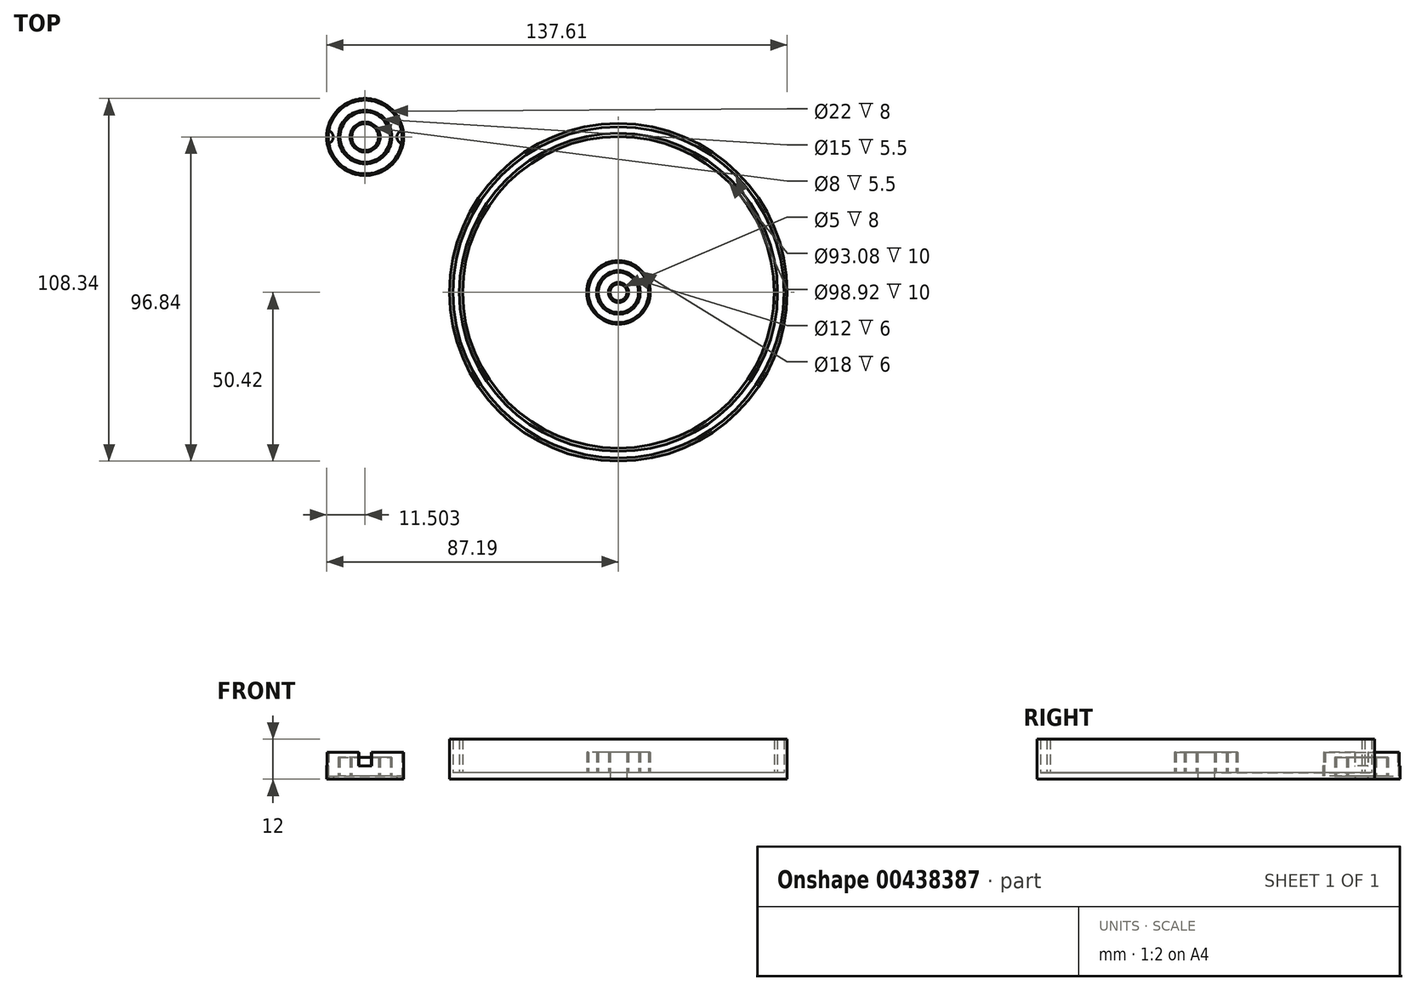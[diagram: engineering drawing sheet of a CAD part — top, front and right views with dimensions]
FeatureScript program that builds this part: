
annotation { "Feature Type Name" : "Feature", "Feature Type Description" : "" }
export const myFeature = defineFeature(function(context is Context, id is Id, definition is map)
    precondition{}
    {
        {
            var Q0;
            Q0=qCreatedBy(makeId("Top.planeOp"),FACE);
            var sketch = newSketch(context, id + "F0", { "sketchPlane" : qUnion([Q0])});
            skCircle(sketch, "E0", {"center": v(0, 0) * mm, "radius": 47.5 * mm});
            skCircle(sketch, "E1", {"center": v(0, 0) * mm, "radius": 49.46 * mm});
            skCircle(sketch, "E2", {"center": v(0, 0) * mm, "radius": 50.42 * mm});
            skCircle(sketch, "E3", {"center": v(0, 0) * mm, "radius": 46.54 * mm});
            skCircle(sketch, "E4", {"center": v(0, 0) * mm, "radius": 2.5 * mm});
            skCircle(sketch, "E5", {"center": v(0, 0) * mm, "radius": 3 * mm});
            skCircle(sketch, "E6", {"center": v(0, 0) * mm, "radius": 6 * mm});
            skCircle(sketch, "E7", {"center": v(0, 0) * mm, "radius": 6.5 * mm});
            skCircle(sketch, "E8", {"center": v(0, 0) * mm, "radius": 9 * mm});
            skCircle(sketch, "E9", {"center": v(0, 0) * mm, "radius": 9.5 * mm});
            skSolve(sketch);
        }
        {
            var Q0;
            Q0=makeQuery(id+"F0.imprint","IMPRINT",FACE,{"disambiguationData":[TD([[makeQuery(id+"F0.imprint","IMPRINT",EDGE,{"derivedFrom":sQuery(id+"F0.wireOp",EDGE,"E0")}),1.0]])]});
            var Q1;
            Q1=makeQuery(id+"F0.imprint","IMPRINT",FACE,{"disambiguationData":[TD([[makeQuery(id+"F0.imprint","IMPRINT",EDGE,{"derivedFrom":sQuery(id+"F0.wireOp",EDGE,"E1")}),-1.0]])]});
            var Q2;
            Q2=makeQuery(id+"F0.imprint","IMPRINT",FACE,{"disambiguationData":[TD([[makeQuery(id+"F0.imprint","IMPRINT",EDGE,{"derivedFrom":sQuery(id+"F0.wireOp",EDGE,"E0")}),-1.0]])]});
            var Q3;
            Q3=makeQuery(id+"F0.imprint","IMPRINT",FACE,{"disambiguationData":[TD([[makeQuery(id+"F0.imprint","IMPRINT",EDGE,{"derivedFrom":sQuery(id+"F0.wireOp",EDGE,"E3")}),1.0]])]});
            var Q4;
            Q4=makeQuery(id+"F0.imprint","IMPRINT",FACE,{"disambiguationData":[TD([[makeQuery(id+"F0.imprint","IMPRINT",EDGE,{"derivedFrom":sQuery(id+"F0.wireOp",EDGE,"E7")}),-1.0]])]});
            var Q5;
            Q5=makeQuery(id+"F0.imprint","IMPRINT",FACE,{"disambiguationData":[TD([[makeQuery(id+"F0.imprint","IMPRINT",EDGE,{"derivedFrom":sQuery(id+"F0.wireOp",EDGE,"E5")}),-1.0]])]});
            var Q6;
            Q6=makeQuery(id+"F0.imprint","IMPRINT",FACE,{"disambiguationData":[TD([[makeQuery(id+"F0.imprint","IMPRINT",EDGE,{"derivedFrom":sQuery(id+"F0.wireOp",EDGE,"E4")}),-1.0]])]});
            var Q7;
            Q7=makeQuery(id+"F0.imprint","IMPRINT",FACE,{"disambiguationData":[TD([[makeQuery(id+"F0.imprint","IMPRINT",EDGE,{"derivedFrom":sQuery(id+"F0.wireOp",EDGE,"E6")}),-1.0]])]});
            var Q8;
            Q8=makeQuery(id+"F0.imprint","IMPRINT",FACE,{"disambiguationData":[TD([[makeQuery(id+"F0.imprint","IMPRINT",EDGE,{"derivedFrom":sQuery(id+"F0.wireOp",EDGE,"E8")}),-1.0]])]});
            extrude(context, id + "F1", {"entities" : qUnion([Q0, Q1, Q2, Q3, Q4, Q5, Q6, Q7, Q8]), "depth" : 2 * mm, "offsetDistance" : 25 * mm});
        }
        {
            var Q0;
            Q0=makeQuery(id+"F0.imprint","IMPRINT",FACE,{"disambiguationData":[TD([[makeQuery(id+"F0.imprint","IMPRINT",EDGE,{"derivedFrom":sQuery(id+"F0.wireOp",EDGE,"E1")}),-1.0]])]});
            var Q1;
            Q1=makeQuery(id+"F0.imprint","IMPRINT",FACE,{"disambiguationData":[TD([[makeQuery(id+"F0.imprint","IMPRINT",EDGE,{"derivedFrom":sQuery(id+"F0.wireOp",EDGE,"E0")}),1.0]])]});
            extrude(context, id + "F2", {"entities" : qUnion([Q0, Q1]), "operationType" : NewBodyOperationType.ADD, "depth" : 12 * mm, "offsetDistance" : 25 * mm});
        }
        {
            var Q0;
            Q0=makeQuery(id+"F0.imprint","IMPRINT",FACE,{"disambiguationData":[TD([[makeQuery(id+"F0.imprint","IMPRINT",EDGE,{"derivedFrom":sQuery(id+"F0.wireOp",EDGE,"E8")}),-1.0]])]});
            var Q1;
            Q1=makeQuery(id+"F0.imprint","IMPRINT",FACE,{"disambiguationData":[TD([[makeQuery(id+"F0.imprint","IMPRINT",EDGE,{"derivedFrom":sQuery(id+"F0.wireOp",EDGE,"E6")}),-1.0]])]});
            var Q2;
            Q2=makeQuery(id+"F0.imprint","IMPRINT",FACE,{"disambiguationData":[TD([[makeQuery(id+"F0.imprint","IMPRINT",EDGE,{"derivedFrom":sQuery(id+"F0.wireOp",EDGE,"E4")}),-1.0]])]});
            extrude(context, id + "F3", {"entities" : qUnion([Q0, Q1, Q2]), "operationType" : NewBodyOperationType.ADD, "depth" : 8 * mm, "offsetDistance" : 25 * mm});
        }
        {
            var Q0;
            Q0=qCreatedBy(makeId("Top.planeOp"),FACE);
            var sketch = newSketch(context, id + "F4", { "sketchPlane" : qUnion([Q0])});
            skCircle(sketch, "E10", {"center": v(-75.69, 46.42) * mm, "radius": 4 * mm});
            skCircle(sketch, "E11", {"center": v(-75.69, 46.42) * mm, "radius": 4.5 * mm});
            skCircle(sketch, "E12", {"center": v(-75.69, 46.42) * mm, "radius": 7.5 * mm});
            skCircle(sketch, "E13", {"center": v(-75.69, 46.42) * mm, "radius": 8 * mm});
            skCircle(sketch, "E14", {"center": v(-75.69, 46.42) * mm, "radius": 11 * mm});
            skCircle(sketch, "E15", {"center": v(-75.69, 46.42) * mm, "radius": 11.5 * mm});
            skCircle(sketch, "E16", {"center": v(-64.19, 46.42) * mm, "radius": 2 * mm});
            skCircle(sketch, "E17", {"center": v(-75.69, 34.92) * mm, "radius": 2 * mm});
            skCircle(sketch, "E18", {"center": v(-87.19, 46.42) * mm, "radius": 2 * mm});
            skCircle(sketch, "E19", {"center": v(-75.69, 57.92) * mm, "radius": 2 * mm});
            skSolve(sketch);
        }
        {
            var Q0;
            Q0=makeQuery(id+"F4.imprint","IMPRINT",FACE,{"disambiguationData":[TD([[makeQuery(id+"F4.imprint","IMPRINT",EDGE,{"derivedFrom":sQuery(id+"F4.wireOp",EDGE,"E11")}),-1.0]])]});
            var Q1;
            Q1=makeQuery(id+"F4.imprint","IMPRINT",FACE,{"disambiguationData":[TD([[makeQuery(id+"F4.imprint","IMPRINT",EDGE,{"derivedFrom":sQuery(id+"F4.wireOp",EDGE,"E10")}),-1.0]])]});
            var Q2;
            Q2=makeQuery(id+"F4.imprint","IMPRINT",FACE,{"disambiguationData":[TD([[makeQuery(id+"F4.imprint","IMPRINT",EDGE,{"derivedFrom":sQuery(id+"F4.wireOp",EDGE,"E10")}),1.0]])]});
            var Q3;
            Q3=makeQuery(id+"F4.imprint","IMPRINT",FACE,{"disambiguationData":[TD([[makeQuery(id+"F4.imprint","IMPRINT",EDGE,{"derivedFrom":sQuery(id+"F4.wireOp",EDGE,"E12")}),-1.0]])]});
            var Q4;
            Q4=makeQuery(id+"F4.imprint","IMPRINT",FACE,{"disambiguationData":[TD([[makeQuery(id+"F4.imprint","IMPRINT",EDGE,{"derivedFrom":sQuery(id+"F4.wireOp",EDGE,"E13")}),-1.0]])]});
            var Q5;
            Q5=makeQuery(id+"F4.imprint","IMPRINT",FACE,{"disambiguationData":[TD([[makeQuery(id+"F4.imprint","IMPRINT",EDGE,{"derivedFrom":sQuery(id+"F4.wireOp",EDGE,"E14")}),-1.0]])]});
            extrude(context, id + "F5", {"entities" : qUnion([Q0, Q1, Q2, Q3, Q4, Q5]), "depth" : 1 * mm, "offsetDistance" : 25 * mm});
        }
        {
            var Q0;
            Q0=makeQuery(id+"F4.imprint","IMPRINT",FACE,{"disambiguationData":[TD([[makeQuery(id+"F4.imprint","IMPRINT",EDGE,{"derivedFrom":sQuery(id+"F4.wireOp",EDGE,"E14")}),-1.0]])]});
            var Q1;
            Q1=makeQuery(id+"F4.imprint","IMPRINT",FACE,{"disambiguationData":[TD([[makeQuery(id+"F4.imprint","IMPRINT",EDGE,{"derivedFrom":sQuery(id+"F4.wireOp",EDGE,"E12")}),-1.0]])]});
            var Q2;
            Q2=makeQuery(id+"F4.imprint","IMPRINT",FACE,{"disambiguationData":[TD([[makeQuery(id+"F4.imprint","IMPRINT",EDGE,{"derivedFrom":sQuery(id+"F4.wireOp",EDGE,"E10")}),-1.0]])]});
            var Q3;
            {var subQ0=sQuery(id+"F4.wireOp",EDGE,"E16");var subQ1=sQuery(id+"F4.wireOp",EDGE,"E14");var subQ2=makeQuery(id+"F4.imprint","INTERSECT",VERTEX,{"disambiguationData":[OD(0.0)],"derivedFrom":[subQ1,subQ0]});Q3=makeQuery(id+"F4.imprint","IMPRINT",FACE,{"disambiguationData":[TD([[makeQuery(id+"F4.imprint","IMPRINT",EDGE,{"disambiguationData":[TD([[subQ2,-1.0]])],"derivedFrom":subQ1}),-1.0]])]});}
            var Q4;
            {var subQ0=sQuery(id+"F4.wireOp",EDGE,"E19");var subQ1=sQuery(id+"F4.wireOp",EDGE,"E14");var subQ2=makeQuery(id+"F4.imprint","INTERSECT",VERTEX,{"disambiguationData":[OD(1.0)],"derivedFrom":[subQ1,subQ0]});Q4=makeQuery(id+"F4.imprint","IMPRINT",FACE,{"disambiguationData":[TD([[makeQuery(id+"F4.imprint","IMPRINT",EDGE,{"disambiguationData":[TD([[subQ2,-1.0]])],"derivedFrom":subQ1}),-1.0]])]});}
            var Q5;
            {var subQ0=sQuery(id+"F4.wireOp",EDGE,"E17");var subQ1=sQuery(id+"F4.wireOp",EDGE,"E14");var subQ2=makeQuery(id+"F4.imprint","INTERSECT",VERTEX,{"disambiguationData":[OD(1.0)],"derivedFrom":[subQ1,subQ0]});Q5=makeQuery(id+"F4.imprint","IMPRINT",FACE,{"disambiguationData":[TD([[makeQuery(id+"F4.imprint","IMPRINT",EDGE,{"disambiguationData":[TD([[subQ2,-1.0]])],"derivedFrom":subQ1}),-1.0]])]});}
            var Q6;
            {var subQ0=sQuery(id+"F4.wireOp",EDGE,"E18");var subQ1=sQuery(id+"F4.wireOp",EDGE,"E14");var subQ2=makeQuery(id+"F4.imprint","INTERSECT",VERTEX,{"disambiguationData":[OD(1.0)],"derivedFrom":[subQ1,subQ0]});Q6=makeQuery(id+"F4.imprint","IMPRINT",FACE,{"disambiguationData":[TD([[makeQuery(id+"F4.imprint","IMPRINT",EDGE,{"disambiguationData":[TD([[subQ2,-1.0]])],"derivedFrom":subQ1}),-1.0]])]});}
            var Q7;
            {var subQ0=sQuery(id+"F4.wireOp",EDGE,"E18");var subQ1=sQuery(id+"F4.wireOp",EDGE,"E14");var subQ2=makeQuery(id+"F4.imprint","INTERSECT",VERTEX,{"disambiguationData":[OD(0.0)],"derivedFrom":[subQ1,subQ0]});Q7=makeQuery(id+"F4.imprint","IMPRINT",FACE,{"disambiguationData":[TD([[makeQuery(id+"F4.imprint","IMPRINT",EDGE,{"disambiguationData":[TD([[subQ2,-1.0]])],"derivedFrom":subQ1}),-1.0]])]});}
            var Q8;
            {var subQ0=sQuery(id+"F4.wireOp",EDGE,"E19");var subQ1=sQuery(id+"F4.wireOp",EDGE,"E14");var subQ2=makeQuery(id+"F4.imprint","INTERSECT",VERTEX,{"disambiguationData":[OD(0.0)],"derivedFrom":[subQ1,subQ0]});Q8=makeQuery(id+"F4.imprint","IMPRINT",FACE,{"disambiguationData":[TD([[makeQuery(id+"F4.imprint","IMPRINT",EDGE,{"disambiguationData":[TD([[subQ2,-1.0]])],"derivedFrom":subQ1}),-1.0]])]});}
            var Q9;
            {var subQ0=sQuery(id+"F4.wireOp",EDGE,"E17");var subQ1=sQuery(id+"F4.wireOp",EDGE,"E14");var subQ2=makeQuery(id+"F4.imprint","INTERSECT",VERTEX,{"disambiguationData":[OD(0.0)],"derivedFrom":[subQ1,subQ0]});Q9=makeQuery(id+"F4.imprint","IMPRINT",FACE,{"disambiguationData":[TD([[makeQuery(id+"F4.imprint","IMPRINT",EDGE,{"disambiguationData":[TD([[subQ2,-1.0]])],"derivedFrom":subQ1}),-1.0]])]});}
            extrude(context, id + "F6", {"entities" : qUnion([Q0, Q1, Q2, Q3, Q4, Q5, Q6, Q7, Q8, Q9]), "operationType" : NewBodyOperationType.ADD, "depth" : 8 * mm, "offsetDistance" : 25 * mm});
        }
        {
            var Q0;
            {var subQ0=sQuery(id+"F4.wireOp",EDGE,"E17");var subQ1=sQuery(id+"F4.wireOp",EDGE,"E14");var subQ2=makeQuery(id+"F4.imprint","INTERSECT",VERTEX,{"disambiguationData":[OD(0.0)],"derivedFrom":[subQ1,subQ0]});Q0=makeQuery(id+"F4.imprint","IMPRINT",FACE,{"disambiguationData":[TD([[makeQuery(id+"F4.imprint","IMPRINT",EDGE,{"disambiguationData":[TD([[subQ2,-1.0]])],"derivedFrom":subQ1}),-1.0]])]});}
            var Q1;
            {var subQ5=sQuery(id+"F4.wireOp",EDGE,"E14");var subQ7=makeQuery(id+"F4.imprint","IMPRINT",VERTEX,{"derivedFrom":subQ5});Q1=makeQuery(id+"F4.imprint","IMPRINT",FACE,{"disambiguationData":[TD([[makeQuery(id+"F4.imprint","IMPRINT",EDGE,{"disambiguationData":[TD([[subQ7,-1.0]])],"derivedFrom":subQ5}),-1.0]])]});}
            var Q2;
            {var subQ0=sQuery(id+"F4.wireOp",EDGE,"E18");var subQ1=sQuery(id+"F4.wireOp",EDGE,"E14");var subQ2=makeQuery(id+"F4.imprint","INTERSECT",VERTEX,{"disambiguationData":[OD(0.0)],"derivedFrom":[subQ1,subQ0]});Q2=makeQuery(id+"F4.imprint","IMPRINT",FACE,{"disambiguationData":[TD([[makeQuery(id+"F4.imprint","IMPRINT",EDGE,{"disambiguationData":[TD([[subQ2,-1.0]])],"derivedFrom":subQ1}),-1.0]])]});}
            var Q3;
            {var subQ0=sQuery(id+"F4.wireOp",EDGE,"E19");var subQ1=sQuery(id+"F4.wireOp",EDGE,"E14");var subQ2=makeQuery(id+"F4.imprint","INTERSECT",VERTEX,{"disambiguationData":[OD(0.0)],"derivedFrom":[subQ1,subQ0]});Q3=makeQuery(id+"F4.imprint","IMPRINT",FACE,{"disambiguationData":[TD([[makeQuery(id+"F4.imprint","IMPRINT",EDGE,{"disambiguationData":[TD([[subQ2,-1.0]])],"derivedFrom":subQ1}),-1.0]])]});}
            extrude(context, id + "F7", {"entities" : qUnion([Q0, Q1, Q2, Q3]), "operationType" : NewBodyOperationType.REMOVE, "depth" : 8 * mm, "offsetDistance" : 25 * mm});
        }
        {
            var Q0;
            Q0=makeQuery(id+"F6.opExtrude","CAP_FACE",FACE,{"disambiguationData":[OSD([sQuery(id+"F4.wireOp",EDGE,"E12"),sQuery(id+"F4.wireOp",EDGE,"E13")])],"isStart":false});
            var Q1;
            Q1=makeQuery(id+"F6.opExtrude","CAP_FACE",FACE,{"disambiguationData":[OSD([sQuery(id+"F4.wireOp",EDGE,"E10"),sQuery(id+"F4.wireOp",EDGE,"E11")])],"isStart":false});
            extrude(context, id + "F8", {"entities" : qUnion([Q0, Q1]), "operationType" : NewBodyOperationType.REMOVE, "oppositeDirection" : true, "depth" : 1.5 * mm, "offsetDistance" : 25 * mm});
        }
        {
            var Q0;
            {var subQ0=sQuery(id+"F4.wireOp",EDGE,"E17");var subQ1=sQuery(id+"F4.wireOp",EDGE,"E14");var subQ2=makeQuery(id+"F4.imprint","INTERSECT",VERTEX,{"disambiguationData":[OD(0.0)],"derivedFrom":[subQ1,subQ0]});Q0=makeQuery(id+"F4.imprint","IMPRINT",FACE,{"disambiguationData":[TD([[makeQuery(id+"F4.imprint","IMPRINT",EDGE,{"disambiguationData":[TD([[subQ2,-1.0]])],"derivedFrom":subQ1}),1.0]])]});}
            var Q1;
            {var subQ0=sQuery(id+"F4.wireOp",EDGE,"E17");var subQ1=sQuery(id+"F4.wireOp",EDGE,"E14");var subQ2=makeQuery(id+"F4.imprint","INTERSECT",VERTEX,{"disambiguationData":[OD(0.0)],"derivedFrom":[subQ1,subQ0]});Q1=makeQuery(id+"F4.imprint","IMPRINT",FACE,{"disambiguationData":[TD([[makeQuery(id+"F4.imprint","IMPRINT",EDGE,{"disambiguationData":[TD([[subQ2,-1.0]])],"derivedFrom":subQ1}),-1.0]])]});}
            var Q2;
            {var subQ0=sQuery(id+"F4.wireOp",EDGE,"E19");var subQ1=sQuery(id+"F4.wireOp",EDGE,"E14");var subQ2=makeQuery(id+"F4.imprint","INTERSECT",VERTEX,{"disambiguationData":[OD(0.0)],"derivedFrom":[subQ1,subQ0]});Q2=makeQuery(id+"F4.imprint","IMPRINT",FACE,{"disambiguationData":[TD([[makeQuery(id+"F4.imprint","IMPRINT",EDGE,{"disambiguationData":[TD([[subQ2,-1.0]])],"derivedFrom":subQ1}),1.0]])]});}
            var Q3;
            {var subQ0=sQuery(id+"F4.wireOp",EDGE,"E19");var subQ1=sQuery(id+"F4.wireOp",EDGE,"E14");var subQ2=makeQuery(id+"F4.imprint","INTERSECT",VERTEX,{"disambiguationData":[OD(0.0)],"derivedFrom":[subQ1,subQ0]});Q3=makeQuery(id+"F4.imprint","IMPRINT",FACE,{"disambiguationData":[TD([[makeQuery(id+"F4.imprint","IMPRINT",EDGE,{"disambiguationData":[TD([[subQ2,-1.0]])],"derivedFrom":subQ1}),-1.0]])]});}
            var Q4;
            {var subQ5=sQuery(id+"F4.wireOp",EDGE,"E14");var subQ7=makeQuery(id+"F4.imprint","IMPRINT",VERTEX,{"derivedFrom":subQ5});Q4=makeQuery(id+"F4.imprint","IMPRINT",FACE,{"disambiguationData":[TD([[makeQuery(id+"F4.imprint","IMPRINT",EDGE,{"disambiguationData":[TD([[subQ7,-1.0]])],"derivedFrom":subQ5}),-1.0]])]});}
            var Q5;
            {var subQ0=sQuery(id+"F4.wireOp",EDGE,"E14");var subQ1=makeQuery(id+"F4.imprint","IMPRINT",VERTEX,{"derivedFrom":subQ0});Q5=makeQuery(id+"F4.imprint","IMPRINT",FACE,{"disambiguationData":[TD([[makeQuery(id+"F4.imprint","IMPRINT",EDGE,{"disambiguationData":[TD([[subQ1,-1.0]])],"derivedFrom":subQ0}),1.0]])]});}
            var Q6;
            {var subQ0=sQuery(id+"F4.wireOp",EDGE,"E18");var subQ1=sQuery(id+"F4.wireOp",EDGE,"E14");var subQ2=makeQuery(id+"F4.imprint","INTERSECT",VERTEX,{"disambiguationData":[OD(0.0)],"derivedFrom":[subQ1,subQ0]});Q6=makeQuery(id+"F4.imprint","IMPRINT",FACE,{"disambiguationData":[TD([[makeQuery(id+"F4.imprint","IMPRINT",EDGE,{"disambiguationData":[TD([[subQ2,-1.0]])],"derivedFrom":subQ1}),-1.0]])]});}
            var Q7;
            {var subQ0=sQuery(id+"F4.wireOp",EDGE,"E18");var subQ4=makeQuery(id+"F4.imprint","IMPRINT",VERTEX,{"derivedFrom":subQ0});Q7=makeQuery(id+"F4.imprint","IMPRINT",FACE,{"disambiguationData":[TD([[makeQuery(id+"F4.imprint","IMPRINT",EDGE,{"disambiguationData":[TD([[subQ4,-1.0]])],"derivedFrom":subQ0}),1.0]])]});}
            extrude(context, id + "F9", {"entities" : qUnion([Q0, Q1, Q2, Q3, Q4, Q5, Q6, Q7]), "operationType" : NewBodyOperationType.ADD, "depth" : 1 * mm, "offsetDistance" : 25 * mm});
        }
        {
            var Q0;
            {var subQ0=sQuery(id+"F4.wireOp",EDGE,"E18");var subQ1=sQuery(id+"F4.wireOp",EDGE,"E14");var subQ2=makeQuery(id+"F4.imprint","INTERSECT",VERTEX,{"disambiguationData":[OD(0.0)],"derivedFrom":[subQ1,subQ0]});Q0=makeQuery(id+"F4.imprint","IMPRINT",FACE,{"disambiguationData":[TD([[makeQuery(id+"F4.imprint","IMPRINT",EDGE,{"disambiguationData":[TD([[subQ2,-1.0]])],"derivedFrom":subQ1}),-1.0]])]});}
            var Q1;
            {var subQ0=sQuery(id+"F4.wireOp",EDGE,"E19");var subQ1=sQuery(id+"F4.wireOp",EDGE,"E14");var subQ2=makeQuery(id+"F4.imprint","INTERSECT",VERTEX,{"disambiguationData":[OD(0.0)],"derivedFrom":[subQ1,subQ0]});Q1=makeQuery(id+"F4.imprint","IMPRINT",FACE,{"disambiguationData":[TD([[makeQuery(id+"F4.imprint","IMPRINT",EDGE,{"disambiguationData":[TD([[subQ2,-1.0]])],"derivedFrom":subQ1}),-1.0]])]});}
            var Q2;
            {var subQ5=sQuery(id+"F4.wireOp",EDGE,"E14");var subQ7=makeQuery(id+"F4.imprint","IMPRINT",VERTEX,{"derivedFrom":subQ5});Q2=makeQuery(id+"F4.imprint","IMPRINT",FACE,{"disambiguationData":[TD([[makeQuery(id+"F4.imprint","IMPRINT",EDGE,{"disambiguationData":[TD([[subQ7,-1.0]])],"derivedFrom":subQ5}),-1.0]])]});}
            var Q3;
            {var subQ0=sQuery(id+"F4.wireOp",EDGE,"E17");var subQ1=sQuery(id+"F4.wireOp",EDGE,"E14");var subQ2=makeQuery(id+"F4.imprint","INTERSECT",VERTEX,{"disambiguationData":[OD(0.0)],"derivedFrom":[subQ1,subQ0]});Q3=makeQuery(id+"F4.imprint","IMPRINT",FACE,{"disambiguationData":[TD([[makeQuery(id+"F4.imprint","IMPRINT",EDGE,{"disambiguationData":[TD([[subQ2,-1.0]])],"derivedFrom":subQ1}),-1.0]])]});}
            extrude(context, id + "F10", {"entities" : qUnion([Q0, Q1, Q2, Q3]), "operationType" : NewBodyOperationType.ADD, "depth" : 4 * mm, "offsetDistance" : 25 * mm});
        }
    });
